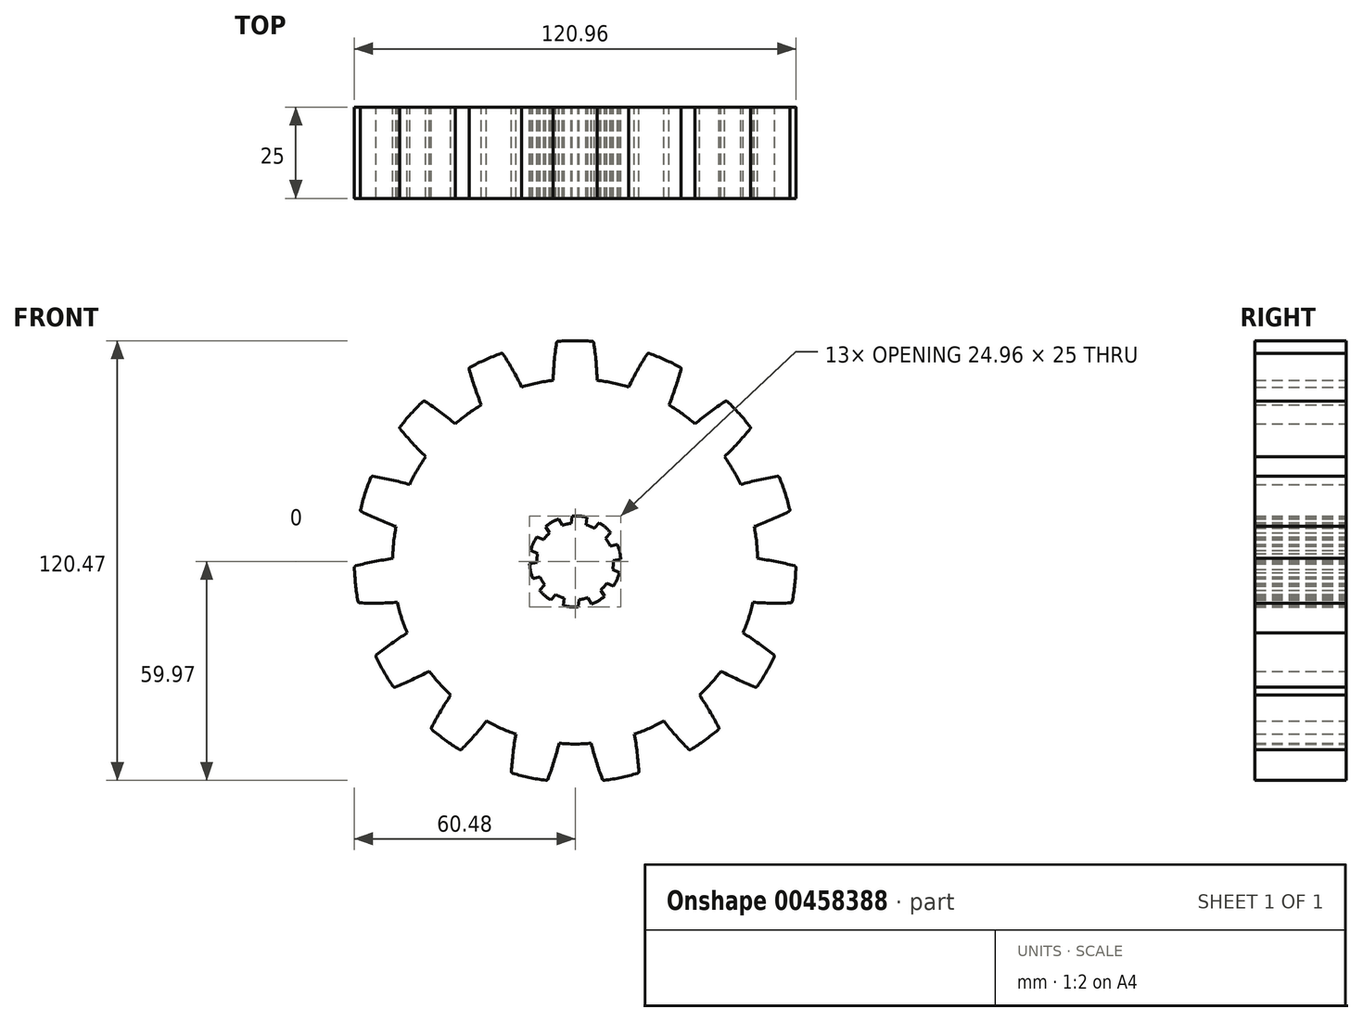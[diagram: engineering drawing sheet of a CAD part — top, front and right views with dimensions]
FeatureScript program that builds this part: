
annotation { "Feature Type Name" : "Feature", "Feature Type Description" : "" }
export const myFeature = defineFeature(function(context is Context, id is Id, definition is map)
    precondition{}
    {
        {
            var Q0;
            Q0=qCreatedBy(makeId("Front.planeOp"),FACE);
            var sketch = newSketch(context, id + "F0", { "sketchPlane" : qUnion([Q0])});
            skCircle(sketch, "E0", {"center": v(0, 0) * mm, "radius": 10.5 * mm});
            skArc(sketch, "E1", {"start": v(-10.5, 6.78) * mm, "mid": v(-11.47, 4.97) * mm, "end": v(-12.13, 3.02) * mm});
            skLineSegment(sketch, "E2", {"start": v(-12.13, 3.02) * mm, "end": v(10.5, -6.78) * mm});
            skLineSegment(sketch, "E3", {"start": v(-10.5, 6.78) * mm, "end": v(12.13, -3.02) * mm});
            skArc(sketch, "E4.trimOffspring", {"start": v(10.5, -6.78) * mm, "mid": v(11.47, -4.97) * mm, "end": v(12.13, -3.02) * mm});
            skArc(sketch, "E5.1.0", {"start": v(-9.7, -7.9) * mm, "mid": v(-8.27, -9.38) * mm, "end": v(-6.62, -10.6) * mm});
            skLineSegment(sketch, "E5.1.1", {"start": v(-9.7, -7.9) * mm, "end": v(6.62, 10.6) * mm});
            skLineSegment(sketch, "E5.1.2", {"start": v(-6.62, -10.6) * mm, "end": v(9.7, 7.9) * mm});
            skArc(sketch, "E5.1.3", {"start": v(9.7, 7.9) * mm, "mid": v(8.27, 9.38) * mm, "end": v(6.62, 10.6) * mm});
            skArc(sketch, "E5.2.0", {"start": v(4.51, -11.66) * mm, "mid": v(6.36, -10.76) * mm, "end": v(8.04, -9.57) * mm});
            skLineSegment(sketch, "E5.2.1", {"start": v(4.51, -11.66) * mm, "end": v(-8.04, 9.57) * mm});
            skLineSegment(sketch, "E5.2.2", {"start": v(8.04, -9.57) * mm, "end": v(-4.51, 11.66) * mm});
            skArc(sketch, "E5.2.3", {"start": v(-4.51, 11.66) * mm, "mid": v(-6.36, 10.76) * mm, "end": v(-8.04, 9.57) * mm});
            skArc(sketch, "E5.3.0", {"start": v(12.48, 0.69) * mm, "mid": v(12.2, 2.73) * mm, "end": v(11.59, 4.69) * mm});
            skLineSegment(sketch, "E5.3.1", {"start": v(12.48, 0.69) * mm, "end": v(-11.59, -4.69) * mm});
            skLineSegment(sketch, "E5.3.2", {"start": v(11.59, 4.69) * mm, "end": v(-12.48, -0.69) * mm});
            skArc(sketch, "E5.3.3", {"start": v(-12.48, -0.69) * mm, "mid": v(-12.2, -2.73) * mm, "end": v(-11.59, -4.69) * mm});
            skArc(sketch, "E5.4.0", {"start": v(3.2, 12.08) * mm, "mid": v(1.18, 12.44) * mm, "end": v(-0.88, 12.47) * mm});
            skLineSegment(sketch, "E5.4.1", {"start": v(3.2, 12.08) * mm, "end": v(0.88, -12.47) * mm});
            skLineSegment(sketch, "E5.4.2", {"start": v(-0.88, 12.47) * mm, "end": v(-3.2, -12.08) * mm});
            skArc(sketch, "E5.4.3", {"start": v(-3.2, -12.08) * mm, "mid": v(-1.18, -12.44) * mm, "end": v(0.88, -12.47) * mm});
            skCircle(sketch, "E6", {"center": v(0, 0) * mm, "radius": 50 * mm});
            skLineSegment(sketch, "E7", {"start": v(0, 46.5) * mm, "end": v(83.9, 46.5) * mm, "construction": true});
            skLineSegment(sketch, "E8", {"start": v(0, 46.5) * mm, "end": v(-83.9, 46.5) * mm, "construction": true});
            skArc(sketch, "E9.trimOffspring", {"start": v(-9.6, -4.27) * mm, "mid": v(-9.58, -4.26) * mm, "end": v(-9.56, -4.24) * mm});
            skArc(sketch, "E10", {"start": v(5.04, 60.29) * mm, "mid": v(0, 60.5) * mm, "end": v(-5.04, 60.29) * mm});
            skArc(sketch, "E11", {"start": v(-5.04, 60.29) * mm, "mid": v(-5.57, 36.78) * mm, "end": v(0, 13.93) * mm});
            skArc(sketch, "E12", {"start": v(-38.88, -31.43) * mm, "mid": v(-19.31, -16.18) * mm, "end": v(-4.65, 3.84) * mm});
            skArc(sketch, "E13.trimOffspring", {"start": v(0, 13.93) * mm, "mid": v(5.57, 36.78) * mm, "end": v(5.04, 60.29) * mm});
            skArc(sketch, "E14.trimOffspring", {"start": v(5, 3.22) * mm, "mid": v(23.42, -20.15) * mm, "end": v(48.46, -36.23) * mm});
            skArc(sketch, "E15.1.0", {"start": v(-29.12, 53.03) * mm, "mid": v(-20.05, 31.33) * mm, "end": v(-5.67, 12.73) * mm});
            skArc(sketch, "E15.1.1", {"start": v(-5.67, 12.73) * mm, "mid": v(-9.87, 35.87) * mm, "end": v(-19.92, 57.13) * mm});
            skArc(sketch, "E15.1.2", {"start": v(-19.92, 57.13) * mm, "mid": v(-24.6, 55.27) * mm, "end": v(-29.12, 53.03) * mm});
            skArc(sketch, "E15.2.0", {"start": v(-48.17, 36.6) * mm, "mid": v(-31.06, 20.47) * mm, "end": v(-10.35, 9.32) * mm});
            skArc(sketch, "E15.2.1", {"start": v(-10.35, 9.32) * mm, "mid": v(-23.6, 28.75) * mm, "end": v(-41.43, 44.09) * mm});
            skArc(sketch, "E15.2.2", {"start": v(-41.43, 44.09) * mm, "mid": v(-44.96, 40.48) * mm, "end": v(-48.17, 36.6) * mm});
            skArc(sketch, "E15.3.0", {"start": v(-58.9, 13.84) * mm, "mid": v(-36.7, 6.06) * mm, "end": v(-13.25, 4.3) * mm});
            skArc(sketch, "E15.3.1", {"start": v(-13.25, 4.3) * mm, "mid": v(-33.26, 16.67) * mm, "end": v(-55.78, 23.42) * mm});
            skArc(sketch, "E15.3.2", {"start": v(-55.78, 23.42) * mm, "mid": v(-57.54, 18.7) * mm, "end": v(-58.9, 13.84) * mm});
            skArc(sketch, "E15.4.0", {"start": v(-59.43, -11.31) * mm, "mid": v(-36, -9.39) * mm, "end": v(-13.85, -1.46) * mm});
            skArc(sketch, "E15.4.1", {"start": v(-13.85, -1.46) * mm, "mid": v(-37.16, 1.7) * mm, "end": v(-60.49, -1.3) * mm});
            skArc(sketch, "E15.4.2", {"start": v(-60.49, -1.3) * mm, "mid": v(-60.17, -6.32) * mm, "end": v(-59.43, -11.31) * mm});
            skArc(sketch, "E15.5.0", {"start": v(-49.7, -34.5) * mm, "mid": v(-29.06, -23.22) * mm, "end": v(-12.06, -6.97) * mm});
            skArc(sketch, "E15.5.1", {"start": v(-12.06, -6.97) * mm, "mid": v(-34.64, -13.56) * mm, "end": v(-54.73, -25.78) * mm});
            skArc(sketch, "E15.5.2", {"start": v(-54.73, -25.78) * mm, "mid": v(-52.4, -30.25) * mm, "end": v(-49.7, -34.5) * mm});
            skArc(sketch, "E15.6.0", {"start": v(-31.36, -51.74) * mm, "mid": v(-17.1, -33.03) * mm, "end": v(-8.19, -11.27) * mm});
            skArc(sketch, "E15.6.1", {"start": v(-8.19, -11.27) * mm, "mid": v(-26.13, -26.48) * mm, "end": v(-39.51, -45.81) * mm});
            skArc(sketch, "E15.6.2", {"start": v(-39.51, -45.81) * mm, "mid": v(-35.56, -48.95) * mm, "end": v(-31.36, -51.74) * mm});
            skArc(sketch, "E15.7.0", {"start": v(-7.6, -60.02) * mm, "mid": v(-2.2, -37.13) * mm, "end": v(-2.9, -13.63) * mm});
            skArc(sketch, "E15.7.1", {"start": v(-2.9, -13.63) * mm, "mid": v(-13.1, -34.82) * mm, "end": v(-17.46, -57.93) * mm});
            skArc(sketch, "E15.7.2", {"start": v(-17.46, -57.93) * mm, "mid": v(-12.58, -59.18) * mm, "end": v(-7.6, -60.02) * mm});
            skArc(sketch, "E15.8.0", {"start": v(17.46, -57.93) * mm, "mid": v(13.1, -34.82) * mm, "end": v(2.9, -13.63) * mm});
            skArc(sketch, "E15.8.1", {"start": v(2.9, -13.63) * mm, "mid": v(2.2, -37.13) * mm, "end": v(7.6, -60.02) * mm});
            skArc(sketch, "E15.8.2", {"start": v(7.6, -60.02) * mm, "mid": v(12.58, -59.18) * mm, "end": v(17.46, -57.93) * mm});
            skArc(sketch, "E15.9.0", {"start": v(39.51, -45.81) * mm, "mid": v(26.13, -26.48) * mm, "end": v(8.19, -11.27) * mm});
            skArc(sketch, "E15.9.1", {"start": v(8.19, -11.27) * mm, "mid": v(17.1, -33.03) * mm, "end": v(31.36, -51.74) * mm});
            skArc(sketch, "E15.9.2", {"start": v(31.36, -51.74) * mm, "mid": v(35.56, -48.95) * mm, "end": v(39.51, -45.81) * mm});
            skArc(sketch, "E16.3.10.0", {"start": v(54.73, -25.78) * mm, "mid": v(34.64, -13.56) * mm, "end": v(12.06, -6.97) * mm});
            skArc(sketch, "E16.4.10.0", {"start": v(12.06, -6.97) * mm, "mid": v(29.06, -23.22) * mm, "end": v(49.7, -34.5) * mm});
            skArc(sketch, "E16.8.10.0", {"start": v(49.7, -34.5) * mm, "mid": v(52.4, -30.25) * mm, "end": v(54.73, -25.78) * mm});
            skArc(sketch, "E16.3.11.0", {"start": v(60.49, -1.3) * mm, "mid": v(37.16, 1.7) * mm, "end": v(13.85, -1.46) * mm});
            skArc(sketch, "E16.4.11.0", {"start": v(13.85, -1.46) * mm, "mid": v(36, -9.39) * mm, "end": v(59.43, -11.31) * mm});
            skArc(sketch, "E16.8.11.0", {"start": v(59.43, -11.31) * mm, "mid": v(60.17, -6.32) * mm, "end": v(60.49, -1.3) * mm});
            skArc(sketch, "E16.3.12.0", {"start": v(55.78, 23.42) * mm, "mid": v(33.26, 16.67) * mm, "end": v(13.25, 4.3) * mm});
            skArc(sketch, "E16.4.12.0", {"start": v(13.25, 4.3) * mm, "mid": v(36.7, 6.06) * mm, "end": v(58.9, 13.84) * mm});
            skArc(sketch, "E16.8.12.0", {"start": v(58.9, 13.84) * mm, "mid": v(57.54, 18.7) * mm, "end": v(55.78, 23.42) * mm});
            skArc(sketch, "E16.3.13.0", {"start": v(41.43, 44.09) * mm, "mid": v(23.6, 28.75) * mm, "end": v(10.35, 9.32) * mm});
            skArc(sketch, "E16.4.13.0", {"start": v(10.35, 9.32) * mm, "mid": v(31.06, 20.47) * mm, "end": v(48.17, 36.6) * mm});
            skArc(sketch, "E16.8.13.0", {"start": v(48.17, 36.6) * mm, "mid": v(44.96, 40.48) * mm, "end": v(41.43, 44.09) * mm});
            skArc(sketch, "E16.3.14.0", {"start": v(19.92, 57.13) * mm, "mid": v(9.87, 35.87) * mm, "end": v(5.67, 12.73) * mm});
            skArc(sketch, "E16.4.14.0", {"start": v(5.67, 12.73) * mm, "mid": v(20.05, 31.33) * mm, "end": v(29.12, 53.03) * mm});
            skArc(sketch, "E16.8.14.0", {"start": v(29.12, 53.03) * mm, "mid": v(24.6, 55.27) * mm, "end": v(19.92, 57.13) * mm});
            skSolve(sketch);
        }
        {
            var Q0;
            Q0 = qSketchRegion(id + "F0", true);
            var Q1;
            {var subQ15=sQuery(id+"F0.wireOp",EDGE,"E1");Q1=makeQuery(id+"F0.imprint","IMPRINT",FACE,{"disambiguationData":[TD([[makeQuery(id+"F0.imprint","IMPRINT",EDGE,{"derivedFrom":subQ15}),-1.0]])]});}
            extrude(context, id + "F1", {"entities" : qUnion([Q0, Q1]), "depth" : 25 * mm, "offsetDistance" : 25 * mm});
        }
        {
            var Q0;
            Q0=makeQuery(id+"F1.opExtrude","SWEPT_EDGE",EDGE,{"disambiguationData":[OSD([sQuery(id+"F0.wireOp",EDGE,"E10"),sQuery(id+"F0.wireOp",EDGE,"E12")])]});
            var Q1;
            Q1=makeQuery(id+"F1.opExtrude","SWEPT_EDGE",EDGE,{"disambiguationData":[OSD([sQuery(id+"F0.wireOp",EDGE,"E10"),sQuery(id+"F0.wireOp",EDGE,"E11")])]});
            var Q2;
            Q2=makeQuery(id+"F1.opExtrude","SWEPT_EDGE",EDGE,{"disambiguationData":[OSD([sQuery(id+"F0.wireOp",EDGE,"E16.3.14.0"),sQuery(id+"F0.wireOp",EDGE,"E16.8.14.0")])]});
            var Q3;
            Q3=makeQuery(id+"F1.opExtrude","SWEPT_EDGE",EDGE,{"disambiguationData":[OSD([sQuery(id+"F0.wireOp",EDGE,"E16.4.14.0"),sQuery(id+"F0.wireOp",EDGE,"E16.8.14.0")])]});
            var Q4;
            Q4=makeQuery(id+"F1.opExtrude","SWEPT_EDGE",EDGE,{"disambiguationData":[OSD([sQuery(id+"F0.wireOp",EDGE,"E16.3.13.0"),sQuery(id+"F0.wireOp",EDGE,"E16.8.13.0")])]});
            var Q5;
            Q5=makeQuery(id+"F1.opExtrude","SWEPT_EDGE",EDGE,{"disambiguationData":[OSD([sQuery(id+"F0.wireOp",EDGE,"E16.4.13.0"),sQuery(id+"F0.wireOp",EDGE,"E16.8.13.0")])]});
            var Q6;
            Q6=makeQuery(id+"F1.opExtrude","SWEPT_EDGE",EDGE,{"disambiguationData":[OSD([sQuery(id+"F0.wireOp",EDGE,"E16.3.12.0"),sQuery(id+"F0.wireOp",EDGE,"E16.8.12.0")])]});
            var Q7;
            Q7=makeQuery(id+"F1.opExtrude","SWEPT_EDGE",EDGE,{"disambiguationData":[OSD([sQuery(id+"F0.wireOp",EDGE,"E16.4.12.0"),sQuery(id+"F0.wireOp",EDGE,"E16.8.12.0")])]});
            var Q8;
            Q8=makeQuery(id+"F1.opExtrude","SWEPT_EDGE",EDGE,{"disambiguationData":[OSD([sQuery(id+"F0.wireOp",EDGE,"E15.1.1"),sQuery(id+"F0.wireOp",EDGE,"E15.1.2")])]});
            var Q9;
            Q9=makeQuery(id+"F1.opExtrude","SWEPT_EDGE",EDGE,{"disambiguationData":[OSD([sQuery(id+"F0.wireOp",EDGE,"E15.1.0"),sQuery(id+"F0.wireOp",EDGE,"E15.1.2")])]});
            var Q10;
            Q10=makeQuery(id+"F1.opExtrude","SWEPT_EDGE",EDGE,{"disambiguationData":[OSD([sQuery(id+"F0.wireOp",EDGE,"E15.2.1"),sQuery(id+"F0.wireOp",EDGE,"E15.2.2")])]});
            var Q11;
            Q11=makeQuery(id+"F1.opExtrude","SWEPT_EDGE",EDGE,{"disambiguationData":[OSD([sQuery(id+"F0.wireOp",EDGE,"E15.2.0"),sQuery(id+"F0.wireOp",EDGE,"E15.2.2")])]});
            var Q12;
            Q12=makeQuery(id+"F1.opExtrude","SWEPT_EDGE",EDGE,{"disambiguationData":[OSD([sQuery(id+"F0.wireOp",EDGE,"E15.3.1"),sQuery(id+"F0.wireOp",EDGE,"E15.3.2")])]});
            var Q13;
            Q13=makeQuery(id+"F1.opExtrude","SWEPT_EDGE",EDGE,{"disambiguationData":[OSD([sQuery(id+"F0.wireOp",EDGE,"E15.3.0"),sQuery(id+"F0.wireOp",EDGE,"E15.3.2")])]});
            var Q14;
            Q14=makeQuery(id+"F1.opExtrude","SWEPT_EDGE",EDGE,{"disambiguationData":[OSD([sQuery(id+"F0.wireOp",EDGE,"E15.4.1"),sQuery(id+"F0.wireOp",EDGE,"E15.4.2")])]});
            var Q15;
            Q15=makeQuery(id+"F1.opExtrude","SWEPT_EDGE",EDGE,{"disambiguationData":[OSD([sQuery(id+"F0.wireOp",EDGE,"E15.4.0"),sQuery(id+"F0.wireOp",EDGE,"E15.4.2")])]});
            var Q16;
            Q16=makeQuery(id+"F1.opExtrude","SWEPT_EDGE",EDGE,{"disambiguationData":[OSD([sQuery(id+"F0.wireOp",EDGE,"E15.5.1"),sQuery(id+"F0.wireOp",EDGE,"E15.5.2")])]});
            var Q17;
            Q17=makeQuery(id+"F1.opExtrude","SWEPT_EDGE",EDGE,{"disambiguationData":[OSD([sQuery(id+"F0.wireOp",EDGE,"E15.5.0"),sQuery(id+"F0.wireOp",EDGE,"E15.5.2")])]});
            var Q18;
            Q18=makeQuery(id+"F1.opExtrude","SWEPT_EDGE",EDGE,{"disambiguationData":[OSD([sQuery(id+"F0.wireOp",EDGE,"E15.6.1"),sQuery(id+"F0.wireOp",EDGE,"E15.6.2")])]});
            var Q19;
            Q19=makeQuery(id+"F1.opExtrude","SWEPT_EDGE",EDGE,{"disambiguationData":[OSD([sQuery(id+"F0.wireOp",EDGE,"E15.6.0"),sQuery(id+"F0.wireOp",EDGE,"E15.6.2")])]});
            var Q20;
            Q20=makeQuery(id+"F1.opExtrude","SWEPT_EDGE",EDGE,{"disambiguationData":[OSD([sQuery(id+"F0.wireOp",EDGE,"E15.7.1"),sQuery(id+"F0.wireOp",EDGE,"E15.7.2")])]});
            var Q21;
            Q21=makeQuery(id+"F1.opExtrude","SWEPT_EDGE",EDGE,{"disambiguationData":[OSD([sQuery(id+"F0.wireOp",EDGE,"E15.7.0"),sQuery(id+"F0.wireOp",EDGE,"E15.7.2")])]});
            var Q22;
            Q22=makeQuery(id+"F1.opExtrude","SWEPT_EDGE",EDGE,{"disambiguationData":[OSD([sQuery(id+"F0.wireOp",EDGE,"E15.8.1"),sQuery(id+"F0.wireOp",EDGE,"E15.8.2")])]});
            var Q23;
            Q23=makeQuery(id+"F1.opExtrude","SWEPT_EDGE",EDGE,{"disambiguationData":[OSD([sQuery(id+"F0.wireOp",EDGE,"E15.8.0"),sQuery(id+"F0.wireOp",EDGE,"E15.8.2")])]});
            var Q24;
            Q24=makeQuery(id+"F1.opExtrude","SWEPT_EDGE",EDGE,{"disambiguationData":[OSD([sQuery(id+"F0.wireOp",EDGE,"E15.9.1"),sQuery(id+"F0.wireOp",EDGE,"E15.9.2")])]});
            var Q25;
            Q25=makeQuery(id+"F1.opExtrude","SWEPT_EDGE",EDGE,{"disambiguationData":[OSD([sQuery(id+"F0.wireOp",EDGE,"E15.9.0"),sQuery(id+"F0.wireOp",EDGE,"E15.9.2")])]});
            var Q26;
            Q26=makeQuery(id+"F1.opExtrude","SWEPT_EDGE",EDGE,{"disambiguationData":[OSD([sQuery(id+"F0.wireOp",EDGE,"E16.4.10.0"),sQuery(id+"F0.wireOp",EDGE,"E16.8.10.0")])]});
            var Q27;
            Q27=makeQuery(id+"F1.opExtrude","SWEPT_EDGE",EDGE,{"disambiguationData":[OSD([sQuery(id+"F0.wireOp",EDGE,"E16.3.10.0"),sQuery(id+"F0.wireOp",EDGE,"E16.8.10.0")])]});
            var Q28;
            Q28=makeQuery(id+"F1.opExtrude","SWEPT_EDGE",EDGE,{"disambiguationData":[OSD([sQuery(id+"F0.wireOp",EDGE,"E16.4.11.0"),sQuery(id+"F0.wireOp",EDGE,"E16.8.11.0")])]});
            var Q29;
            Q29=makeQuery(id+"F1.opExtrude","SWEPT_EDGE",EDGE,{"disambiguationData":[OSD([sQuery(id+"F0.wireOp",EDGE,"E16.3.11.0"),sQuery(id+"F0.wireOp",EDGE,"E16.8.11.0")])]});
            fillet(context, id + "F2", {"entities" : qUnion([Q0, Q1, Q2, Q3, Q4, Q5, Q6, Q7, Q8, Q9, Q10, Q11, Q12, Q13, Q14, Q15, Q16, Q17, Q18, Q19, Q20, Q21, Q22, Q23, Q24, Q25, Q26, Q27, Q28, Q29]), "radius" : 0.5 * mm, "tangentPropagation" : true, "allowEdgeOverflow" : false});
        }
    });
